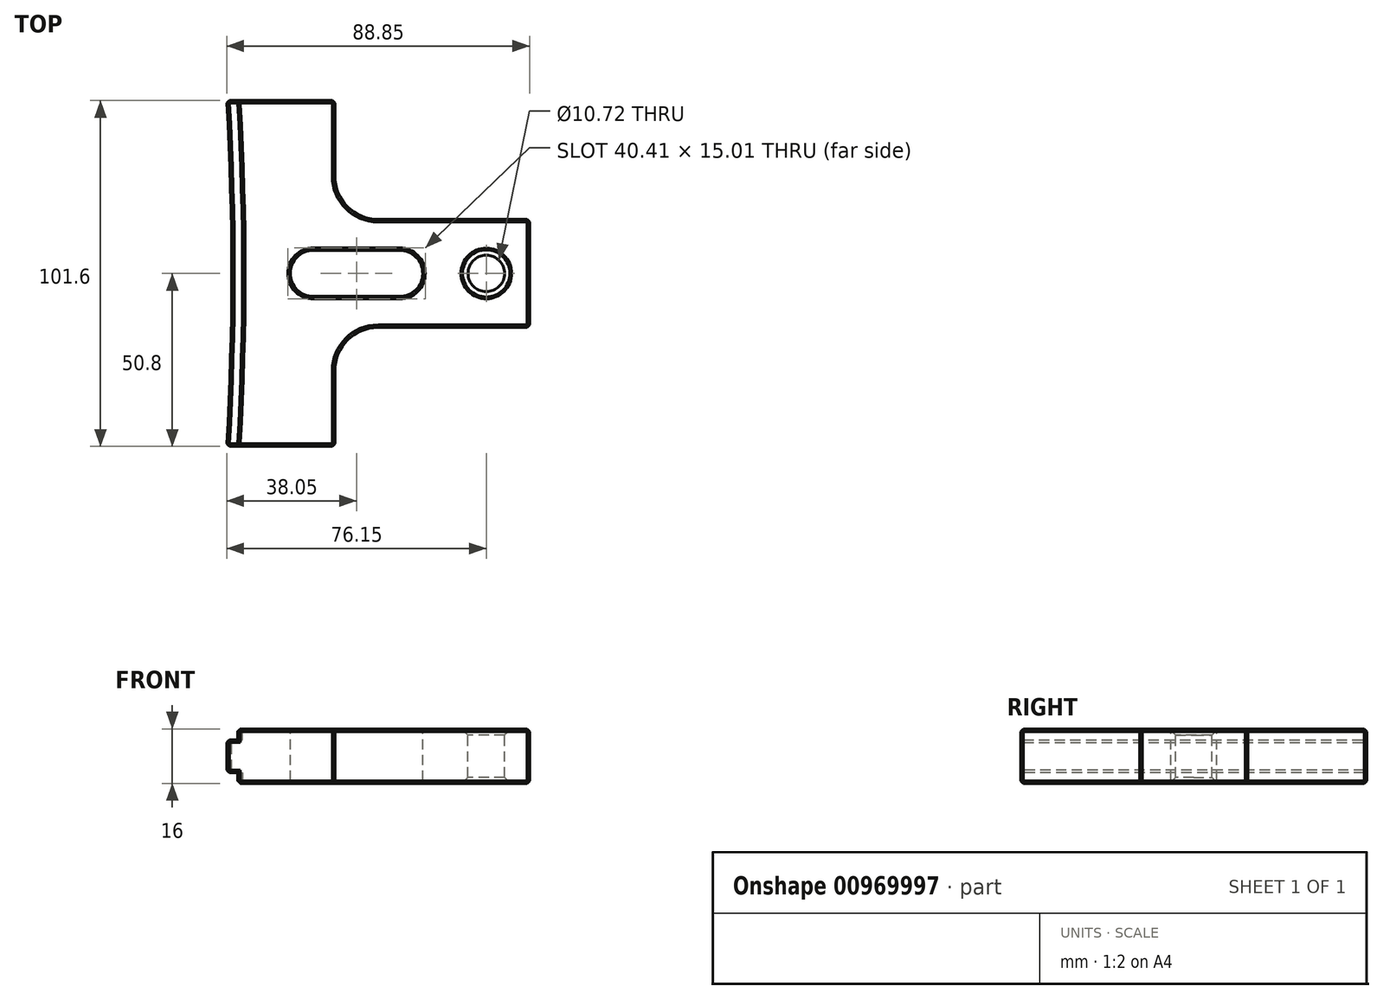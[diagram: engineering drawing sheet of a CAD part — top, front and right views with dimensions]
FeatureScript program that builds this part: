
annotation { "Feature Type Name" : "Feature", "Feature Type Description" : "" }
export const myFeature = defineFeature(function(context is Context, id is Id, definition is map)
    precondition{}
    {
        {
            var Q0;
            Q0=qCreatedBy(makeId("Top.planeOp"),FACE);
            var sketch = newSketch(context, id + "F0", { "sketchPlane" : qUnion([Q0])});
            skLineSegment(sketch, "E0", {"start": v(0, 0) * mm, "end": v(0, 15.88) * mm});
            skLineSegment(sketch, "E1", {"start": v(0, 15.88) * mm, "end": v(-44.45, 15.88) * mm});
            skLineSegment(sketch, "E2", {"start": v(-57.15, 28.57) * mm, "end": v(-57.15, 50.8) * mm});
            skLineSegment(sketch, "E3", {"start": v(-57.15, 50.8) * mm, "end": v(-88.9, 50.8) * mm});
            skLineSegment(sketch, "E4", {"start": v(-88.9, -50.8) * mm, "end": v(-57.15, -50.8) * mm});
            skLineSegment(sketch, "E5", {"start": v(-57.15, -50.8) * mm, "end": v(-57.15, -28.58) * mm});
            skLineSegment(sketch, "E6", {"start": v(-44.45, -15.88) * mm, "end": v(0, -15.88) * mm});
            skLineSegment(sketch, "E7", {"start": v(0, -15.88) * mm, "end": v(0, 0) * mm});
            skPoint(sketch, "E8", {"position": v(-12.7, 0) * mm});
            skPoint(sketch, "E9", {"position": v(-38.1, 0) * mm});
            skPoint(sketch, "E10", {"position": v(-63.5, 0) * mm});
            skPoint(sketch, "E11", {"position": v(-960.55, 0) * mm});
            skArc(sketch, "E12", {"start": v(-88.9, -50.8) * mm, "mid": v(-87.42, 0) * mm, "end": v(-88.9, 50.8) * mm});
            skCircle(sketch, "E13", {"center": v(-63.5, 0) * mm, "radius": 6.74 * mm});
            skCircle(sketch, "E14", {"center": v(-38.1, 0) * mm, "radius": 6.74 * mm});
            skCircle(sketch, "E15", {"center": v(-12.7, 0) * mm, "radius": 5.36 * mm});
            skPoint(sketch, "E16.visualSharp", {"position": v(-57.15, 15.88) * mm});
            skArc(sketch, "E16.filletArc", {"start": v(-57.15, 28.57) * mm, "mid": v(-53.43, 19.6) * mm, "end": v(-44.45, 15.87) * mm});
            skPoint(sketch, "E17.visualSharp", {"position": v(-57.15, -15.88) * mm});
            skArc(sketch, "E17.filletArc", {"start": v(-44.45, -15.88) * mm, "mid": v(-53.43, -19.6) * mm, "end": v(-57.15, -28.57) * mm});
            skLineSegment(sketch, "E18", {"start": v(-63.5, 6.74) * mm, "end": v(-38.1, 6.74) * mm});
            skLineSegment(sketch, "E19", {"start": v(-63.5, -6.74) * mm, "end": v(-38.1, -6.74) * mm});
            skSolve(sketch);
        }
        {
            var Q0;
            Q0 = qSketchRegion(id + "F0", true);
            extrude(context, id + "F1", {"entities" : qUnion([Q0]), "oppositeDirection" : true, "depth" : 16 * mm, "offsetDistance" : 25.4 * mm});
        }
        {
            var Q0;
            Q0=makeQuery(id+"F1.opExtrude","CAP_FACE",FACE,{"disambiguationData":[OSD([sQuery(id+"F0.wireOp",EDGE,"E0"),sQuery(id+"F0.wireOp",EDGE,"E1"),sQuery(id+"F0.wireOp",EDGE,"E2"),sQuery(id+"F0.wireOp",EDGE,"E3"),sQuery(id+"F0.wireOp",EDGE,"E4"),sQuery(id+"F0.wireOp",EDGE,"E5"),sQuery(id+"F0.wireOp",EDGE,"E6"),sQuery(id+"F0.wireOp",EDGE,"E7"),sQuery(id+"F0.wireOp",EDGE,"E12"),sQuery(id+"F0.wireOp",EDGE,"E13"),sQuery(id+"F0.wireOp",EDGE,"E14"),sQuery(id+"F0.wireOp",EDGE,"E15"),sQuery(id+"F0.wireOp",EDGE,"E16.filletArc"),sQuery(id+"F0.wireOp",EDGE,"E17.filletArc")])],"isStart":true});
            var sketch = newSketch(context, id + "F2", { "sketchPlane" : qUnion([Q0])});
            skCircle(sketch, "E20", {"center": v(-960.55, 0) * mm, "radius": 876.3 * mm});
            skSolve(sketch);
        }
        {
            var Q0;
            Q0 = qSketchRegion(id + "F2", true);
            extrude(context, id + "F3", {"entities" : qUnion([Q0]), "operationType" : NewBodyOperationType.REMOVE, "oppositeDirection" : true, "depth" : 3.17 * mm, "offsetDistance" : 25.4 * mm});
        }
        {
            var Q0;
            Q0=makeQuery(id+"F1.opExtrude","CAP_FACE",FACE,{"disambiguationData":[OSD([sQuery(id+"F0.wireOp",EDGE,"E0"),sQuery(id+"F0.wireOp",EDGE,"E1"),sQuery(id+"F0.wireOp",EDGE,"E2"),sQuery(id+"F0.wireOp",EDGE,"E3"),sQuery(id+"F0.wireOp",EDGE,"E4"),sQuery(id+"F0.wireOp",EDGE,"E5"),sQuery(id+"F0.wireOp",EDGE,"E6"),sQuery(id+"F0.wireOp",EDGE,"E7"),sQuery(id+"F0.wireOp",EDGE,"E12"),sQuery(id+"F0.wireOp",EDGE,"E13"),sQuery(id+"F0.wireOp",EDGE,"E14"),sQuery(id+"F0.wireOp",EDGE,"E15"),sQuery(id+"F0.wireOp",EDGE,"E16.filletArc"),sQuery(id+"F0.wireOp",EDGE,"E17.filletArc")])],"isStart":false});
            var sketch = newSketch(context, id + "F4", { "sketchPlane" : qUnion([Q0])});
            skCircle(sketch, "E21", {"center": v(-960.55, 0) * mm, "radius": 876.3 * mm});
            skSolve(sketch);
        }
        {
            var Q0;
            Q0 = qSketchRegion(id + "F4", true);
            extrude(context, id + "F5", {"entities" : qUnion([Q0]), "operationType" : NewBodyOperationType.REMOVE, "oppositeDirection" : true, "depth" : 3.17 * mm, "offsetDistance" : 25.4 * mm});
        }
        {
            var Q0;
            Q0=makeQuery(id+"F1.opExtrude","SWEPT_FACE",FACE,{"disambiguationData":[OSD([sQuery(id+"F0.wireOp",EDGE,"E15")])]});
            chamfer(context, id + "F6", {"entities" : qUnion([Q0]), "width" : 1.78 * mm, "tangentPropagation" : true});
        }
        {
            var Q0;
            Q0=makeQuery(id+"F3.boolean.opBoolean","INTERSECT",EDGE,{"derivedFrom":[makeQuery(id+"F1.opExtrude","SWEPT_FACE",FACE,{"disambiguationData":[OSD([sQuery(id+"F0.wireOp",EDGE,"E4")])]}),makeQuery(id+"F3.opExtrude","SWEPT_FACE",FACE,{"disambiguationData":[OSD([sQuery(id+"F2.wireOp",EDGE,"E20")])]})]});
            var Q1;
            Q1=makeQuery(id+"F3.boolean.opBoolean","INTERSECT",EDGE,{"derivedFrom":[makeQuery(id+"F1.opExtrude","SWEPT_FACE",FACE,{"disambiguationData":[OSD([sQuery(id+"F0.wireOp",EDGE,"E4")])]}),makeQuery(id+"F3.opExtrude","CAP_FACE",FACE,{"disambiguationData":[OSD([sQuery(id+"F2.wireOp",EDGE,"E20")])],"isStart":false})]});
            var Q2;
            Q2=makeQuery(id+"F1.opExtrude","SWEPT_EDGE",EDGE,{"disambiguationData":[OSD([sQuery(id+"F0.wireOp",EDGE,"E4"),sQuery(id+"F0.wireOp",EDGE,"E12")])]});
            var Q3;
            Q3=makeQuery(id+"F5.boolean.opBoolean","INTERSECT",EDGE,{"derivedFrom":[makeQuery(id+"F1.opExtrude","SWEPT_FACE",FACE,{"disambiguationData":[OSD([sQuery(id+"F0.wireOp",EDGE,"E4")])]}),makeQuery(id+"F5.opExtrude","CAP_FACE",FACE,{"disambiguationData":[OSD([sQuery(id+"F4.wireOp",EDGE,"E21")])],"isStart":false})]});
            var Q4;
            Q4=makeQuery(id+"F5.boolean.opBoolean","INTERSECT",EDGE,{"derivedFrom":[makeQuery(id+"F1.opExtrude","SWEPT_FACE",FACE,{"disambiguationData":[OSD([sQuery(id+"F0.wireOp",EDGE,"E4")])]}),makeQuery(id+"F5.opExtrude","SWEPT_FACE",FACE,{"disambiguationData":[OSD([sQuery(id+"F4.wireOp",EDGE,"E21")])]})]});
            var Q5;
            Q5=makeQuery(id+"F3.boolean.opBoolean","INTERSECT",EDGE,{"derivedFrom":[makeQuery(id+"F1.opExtrude","SWEPT_FACE",FACE,{"disambiguationData":[OSD([sQuery(id+"F0.wireOp",EDGE,"E12")])]}),makeQuery(id+"F3.opExtrude","CAP_FACE",FACE,{"disambiguationData":[OSD([sQuery(id+"F2.wireOp",EDGE,"E20")])],"isStart":false})]});
            var Q6;
            Q6=makeQuery(id+"F5.boolean.opBoolean","INTERSECT",EDGE,{"derivedFrom":[makeQuery(id+"F1.opExtrude","SWEPT_FACE",FACE,{"disambiguationData":[OSD([sQuery(id+"F0.wireOp",EDGE,"E12")])]}),makeQuery(id+"F5.opExtrude","CAP_FACE",FACE,{"disambiguationData":[OSD([sQuery(id+"F4.wireOp",EDGE,"E21")])],"isStart":false})]});
            var Q7;
            Q7=makeQuery(id+"F1.opExtrude","SWEPT_EDGE",EDGE,{"disambiguationData":[OSD([sQuery(id+"F0.wireOp",EDGE,"E4"),sQuery(id+"F0.wireOp",EDGE,"E5")])]});
            var Q8;
            Q8=makeQuery(id+"F1.opExtrude","SWEPT_EDGE",EDGE,{"disambiguationData":[OSD([sQuery(id+"F0.wireOp",EDGE,"E6"),sQuery(id+"F0.wireOp",EDGE,"E7")])]});
            var Q9;
            Q9=makeQuery(id+"F1.opExtrude","SWEPT_EDGE",EDGE,{"disambiguationData":[OSD([sQuery(id+"F0.wireOp",EDGE,"E0"),sQuery(id+"F0.wireOp",EDGE,"E1")])]});
            var Q10;
            Q10=makeQuery(id+"F1.opExtrude","SWEPT_EDGE",EDGE,{"disambiguationData":[OSD([sQuery(id+"F0.wireOp",EDGE,"E2"),sQuery(id+"F0.wireOp",EDGE,"E3")])]});
            var Q11;
            Q11=makeQuery(id+"F3.boolean.opBoolean","INTERSECT",EDGE,{"derivedFrom":[makeQuery(id+"F1.opExtrude","SWEPT_FACE",FACE,{"disambiguationData":[OSD([sQuery(id+"F0.wireOp",EDGE,"E3")])]}),makeQuery(id+"F3.opExtrude","SWEPT_FACE",FACE,{"disambiguationData":[OSD([sQuery(id+"F2.wireOp",EDGE,"E20")])]})]});
            var Q12;
            Q12=makeQuery(id+"F3.boolean.opBoolean","INTERSECT",EDGE,{"derivedFrom":[makeQuery(id+"F1.opExtrude","SWEPT_FACE",FACE,{"disambiguationData":[OSD([sQuery(id+"F0.wireOp",EDGE,"E3")])]}),makeQuery(id+"F3.opExtrude","CAP_FACE",FACE,{"disambiguationData":[OSD([sQuery(id+"F2.wireOp",EDGE,"E20")])],"isStart":false})]});
            var Q13;
            Q13=makeQuery(id+"F1.opExtrude","SWEPT_EDGE",EDGE,{"disambiguationData":[OSD([sQuery(id+"F0.wireOp",EDGE,"E3"),sQuery(id+"F0.wireOp",EDGE,"E12")])]});
            var Q14;
            Q14=makeQuery(id+"F5.boolean.opBoolean","INTERSECT",EDGE,{"derivedFrom":[makeQuery(id+"F1.opExtrude","SWEPT_FACE",FACE,{"disambiguationData":[OSD([sQuery(id+"F0.wireOp",EDGE,"E3")])]}),makeQuery(id+"F5.opExtrude","CAP_FACE",FACE,{"disambiguationData":[OSD([sQuery(id+"F4.wireOp",EDGE,"E21")])],"isStart":false})]});
            var Q15;
            Q15=makeQuery(id+"F5.boolean.opBoolean","INTERSECT",EDGE,{"derivedFrom":[makeQuery(id+"F1.opExtrude","SWEPT_FACE",FACE,{"disambiguationData":[OSD([sQuery(id+"F0.wireOp",EDGE,"E3")])]}),makeQuery(id+"F5.opExtrude","SWEPT_FACE",FACE,{"disambiguationData":[OSD([sQuery(id+"F4.wireOp",EDGE,"E21")])]})]});
            chamfer(context, id + "F7", {"entities" : qUnion([Q0, Q1, Q2, Q3, Q4, Q5, Q6, Q7, Q8, Q9, Q10, Q11, Q12, Q13, Q14, Q15]), "width" : 0.76 * mm, "tangentPropagation" : true});
        }
        {
            var Q0;
            Q0=makeQuery(id+"F1.opExtrude","CAP_FACE",FACE,{"disambiguationData":[OSD([sQuery(id+"F0.wireOp",EDGE,"E0"),sQuery(id+"F0.wireOp",EDGE,"E1"),sQuery(id+"F0.wireOp",EDGE,"E2"),sQuery(id+"F0.wireOp",EDGE,"E3"),sQuery(id+"F0.wireOp",EDGE,"E4"),sQuery(id+"F0.wireOp",EDGE,"E5"),sQuery(id+"F0.wireOp",EDGE,"E6"),sQuery(id+"F0.wireOp",EDGE,"E7"),sQuery(id+"F0.wireOp",EDGE,"E12"),sQuery(id+"F0.wireOp",EDGE,"E13"),sQuery(id+"F0.wireOp",EDGE,"E14"),sQuery(id+"F0.wireOp",EDGE,"E15"),sQuery(id+"F0.wireOp",EDGE,"E16.filletArc"),sQuery(id+"F0.wireOp",EDGE,"E17.filletArc")])],"isStart":true});
            var Q1;
            Q1=makeQuery(id+"F1.opExtrude","CAP_FACE",FACE,{"disambiguationData":[OSD([sQuery(id+"F0.wireOp",EDGE,"E0"),sQuery(id+"F0.wireOp",EDGE,"E1"),sQuery(id+"F0.wireOp",EDGE,"E2"),sQuery(id+"F0.wireOp",EDGE,"E3"),sQuery(id+"F0.wireOp",EDGE,"E4"),sQuery(id+"F0.wireOp",EDGE,"E5"),sQuery(id+"F0.wireOp",EDGE,"E6"),sQuery(id+"F0.wireOp",EDGE,"E7"),sQuery(id+"F0.wireOp",EDGE,"E12"),sQuery(id+"F0.wireOp",EDGE,"E13"),sQuery(id+"F0.wireOp",EDGE,"E14"),sQuery(id+"F0.wireOp",EDGE,"E15"),sQuery(id+"F0.wireOp",EDGE,"E16.filletArc"),sQuery(id+"F0.wireOp",EDGE,"E17.filletArc")])],"isStart":false});
            chamfer(context, id + "F8", {"entities" : qUnion([Q0, Q1]), "width" : 0.76 * mm, "tangentPropagation" : true});
        }
    });
